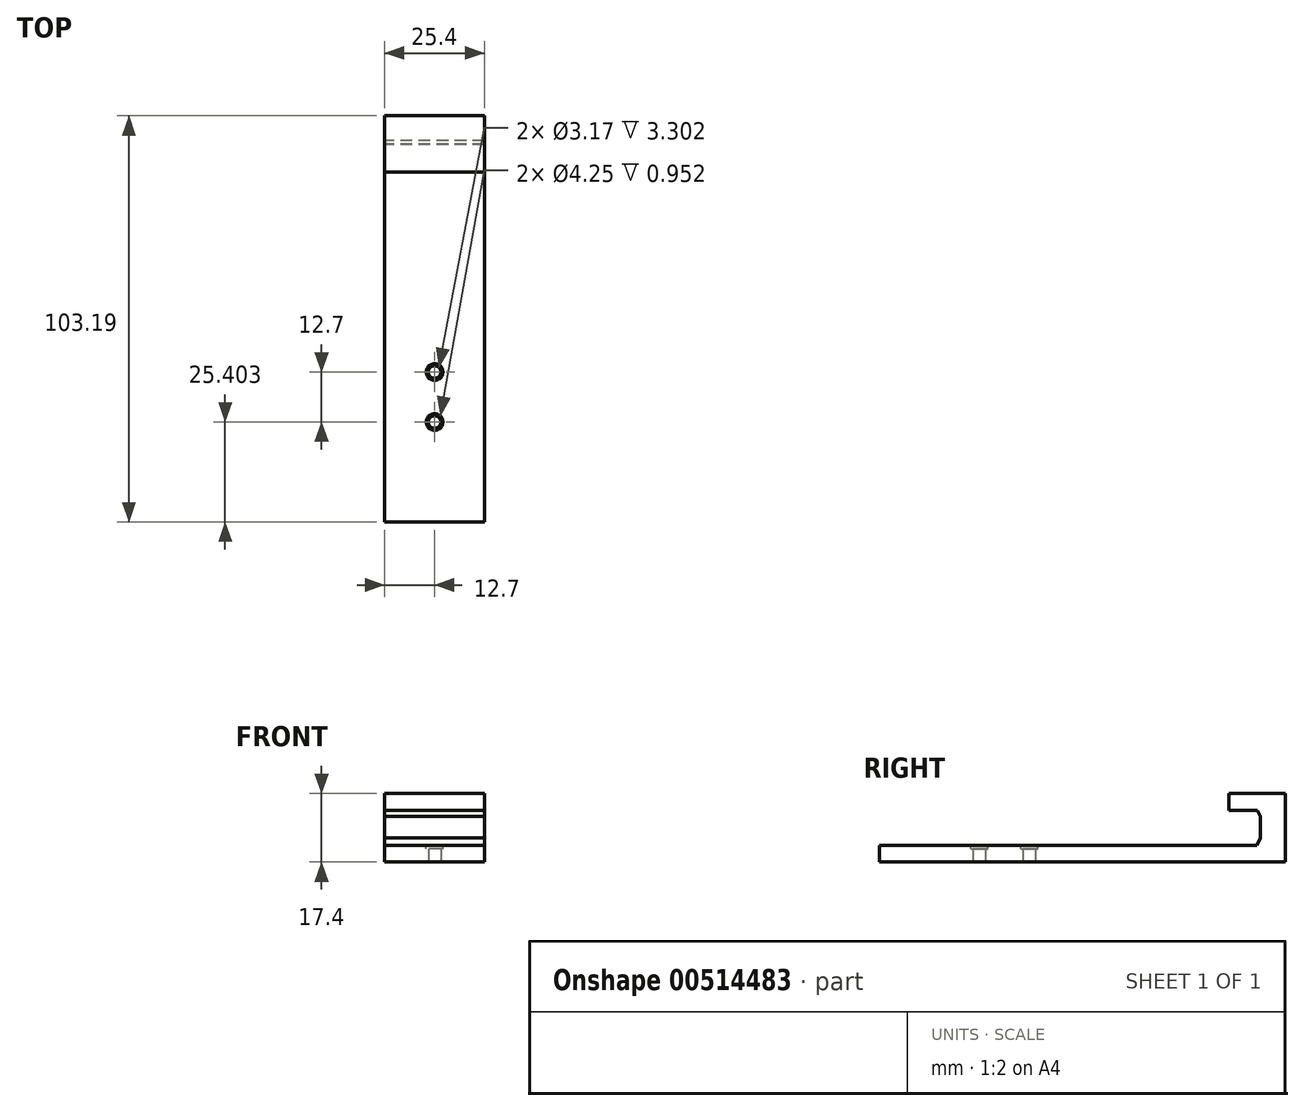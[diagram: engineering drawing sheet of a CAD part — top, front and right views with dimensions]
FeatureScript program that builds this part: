
annotation { "Feature Type Name" : "Feature", "Feature Type Description" : "" }
export const myFeature = defineFeature(function(context is Context, id is Id, definition is map)
    precondition{}
    {
        {
            var Q0;
            Q0=qCreatedBy(makeId("Right.planeOp"),FACE);
            var sketch = newSketch(context, id + "F0", { "sketchPlane" : qUnion([Q0])});
            skLineSegment(sketch, "E0.bottom", {"start": v(0, 0) * mm, "end": v(19.05, 0) * mm});
            skLineSegment(sketch, "E0.top", {"start": v(0, 4.25) * mm, "end": v(11.77, 4.25) * mm});
            skLineSegment(sketch, "E0.left", {"start": v(0, 0) * mm, "end": v(0, 4.25) * mm});
            skLineSegment(sketch, "E0.right", {"start": v(19.05, 0) * mm, "end": v(19.05, 4.25) * mm});
            skLineSegment(sketch, "E1.left", {"start": v(19.05, 4.25) * mm, "end": v(19.05, 17.1) * mm});
            skLineSegment(sketch, "E1.right", {"start": v(12.7, 6.1) * mm, "end": v(12.7, 11.56) * mm});
            skLineSegment(sketch, "E2.bottom", {"start": v(11.87, 13.14) * mm, "end": v(4.7, 13.14) * mm});
            skLineSegment(sketch, "E2.top", {"start": v(19.05, 17.4) * mm, "end": v(4.7, 17.4) * mm});
            skLineSegment(sketch, "E2.left", {"start": v(19.05, 17.1) * mm, "end": v(19.05, 17.4) * mm});
            skLineSegment(sketch, "E2.right", {"start": v(4.7, 13.14) * mm, "end": v(4.7, 17.4) * mm});
            skLineSegment(sketch, "E3", {"start": v(11.87, 13.14) * mm, "end": v(12.7, 11.56) * mm});
            skLineSegment(sketch, "E4", {"start": v(11.77, 4.25) * mm, "end": v(12.7, 6.1) * mm});
            skPoint(sketch, "E5.orphan", {"position": v(19.05, 13.14) * mm});
            skSolve(sketch);
        }
        {
            var Q0;
            Q0=makeQuery(id+"F0.imprint","IMPRINT",FACE,{"disambiguationData":[TD([[makeQuery(id+"F0.imprint","IMPRINT",EDGE,{"derivedFrom":sQuery(id+"F0.wireOp",EDGE,"E0.bottom")}),1.0]])]});
            extrude(context, id + "F1", {"entities" : qUnion([Q0]), "depth" : 25.4 * mm});
        }
        {
            var Q0;
            Q0=makeQuery(id+"F1.opExtrude","SWEPT_FACE",FACE,{"disambiguationData":[OSD([sQuery(id+"F0.wireOp",EDGE,"E0.left")])]});
            extrude(context, id + "F2", {"entities" : qUnion([Q0]), "operationType" : NewBodyOperationType.ADD, "depth" : 84.14 * mm});
        }
        {
            var Q0;
            {var subQ0=sQuery(id+"F0.wireOp",EDGE,"E0.bottom");Q0=makeQuery(id+"F2.boolean.opBoolean","MERGE",FACE,{"derivedFrom":[makeQuery(id+"F1.opExtrude","SWEPT_FACE",FACE,{"disambiguationData":[OSD([subQ0])]}),makeQuery(id+"F2.opExtrude","SWEPT_FACE",FACE,{"disambiguationData":[OSD([subQ0,sQuery(id+"F0.wireOp",EDGE,"E0.left")])]})]});}
            var sketch = newSketch(context, id + "F3", { "sketchPlane" : qUnion([Q0])});
            skCircle(sketch, "E6", {"center": v(12.7, 58.74) * mm, "radius": 1.59 * mm});
            skCircle(sketch, "E7", {"center": v(12.7, 46.04) * mm, "radius": 1.59 * mm});
            skPoint(sketch, "E8.right.start.orphan", {"position": v(15.88, 58.74) * mm});
            skPoint(sketch, "E9.orphan", {"position": v(15.88, 46.04) * mm});
            skPoint(sketch, "E8.left.end.orphan", {"position": v(9.53, 46.04) * mm});
            skPoint(sketch, "E8.left.start.orphan", {"position": v(9.53, 58.74) * mm});
            skSolve(sketch);
        }
        {
            var Q0;
            Q0=makeQuery(id+"F3.imprint","IMPRINT",FACE,{"disambiguationData":[TD([[makeQuery(id+"F3.imprint","IMPRINT",EDGE,{"derivedFrom":sQuery(id+"F3.wireOp",EDGE,"E6")}),1.0]])]});
            var Q1;
            Q1=makeQuery(id+"F3.imprint","IMPRINT",FACE,{"disambiguationData":[TD([[makeQuery(id+"F3.imprint","IMPRINT",EDGE,{"derivedFrom":sQuery(id+"F3.wireOp",EDGE,"E7")}),1.0]])]});
            extrude(context, id + "F4", {"entities" : qUnion([Q0, Q1]), "operationType" : NewBodyOperationType.REMOVE, "oppositeDirection" : true, "depth" : 25.4 * mm});
        }
        {
            var Q0;
            {var subQ0=sQuery(id+"F0.wireOp",EDGE,"E0.top");Q0=makeQuery(id+"F2.boolean.opBoolean","MERGE",FACE,{"derivedFrom":[makeQuery(id+"F1.opExtrude","SWEPT_FACE",FACE,{"disambiguationData":[OSD([subQ0])]}),makeQuery(id+"F2.opExtrude","SWEPT_FACE",FACE,{"disambiguationData":[OSD([subQ0,sQuery(id+"F0.wireOp",EDGE,"E0.left")])]})]});}
            var sketch = newSketch(context, id + "F5", { "sketchPlane" : qUnion([Q0])});
            skCircle(sketch, "E10", {"center": v(12.7, -46.04) * mm, "radius": 2.13 * mm});
            skCircle(sketch, "E11", {"center": v(12.7, -58.74) * mm, "radius": 2.13 * mm});
            skSolve(sketch);
        }
        {
            var Q0;
            Q0=makeQuery(id+"F5.imprint","IMPRINT",FACE,{"disambiguationData":[TD([[makeQuery(id+"F5.imprint","IMPRINT",EDGE,{"derivedFrom":sQuery(id+"F5.wireOp",EDGE,"E10")}),1.0]])]});
            var Q1;
            Q1=makeQuery(id+"F5.imprint","IMPRINT",FACE,{"disambiguationData":[TD([[makeQuery(id+"F5.imprint","IMPRINT",EDGE,{"derivedFrom":sQuery(id+"F5.wireOp",EDGE,"E11")}),1.0]])]});
            extrude(context, id + "F6", {"entities" : qUnion([Q0, Q1]), "operationType" : NewBodyOperationType.REMOVE, "oppositeDirection" : true, "depth" : 0.95 * mm});
        }
    });
